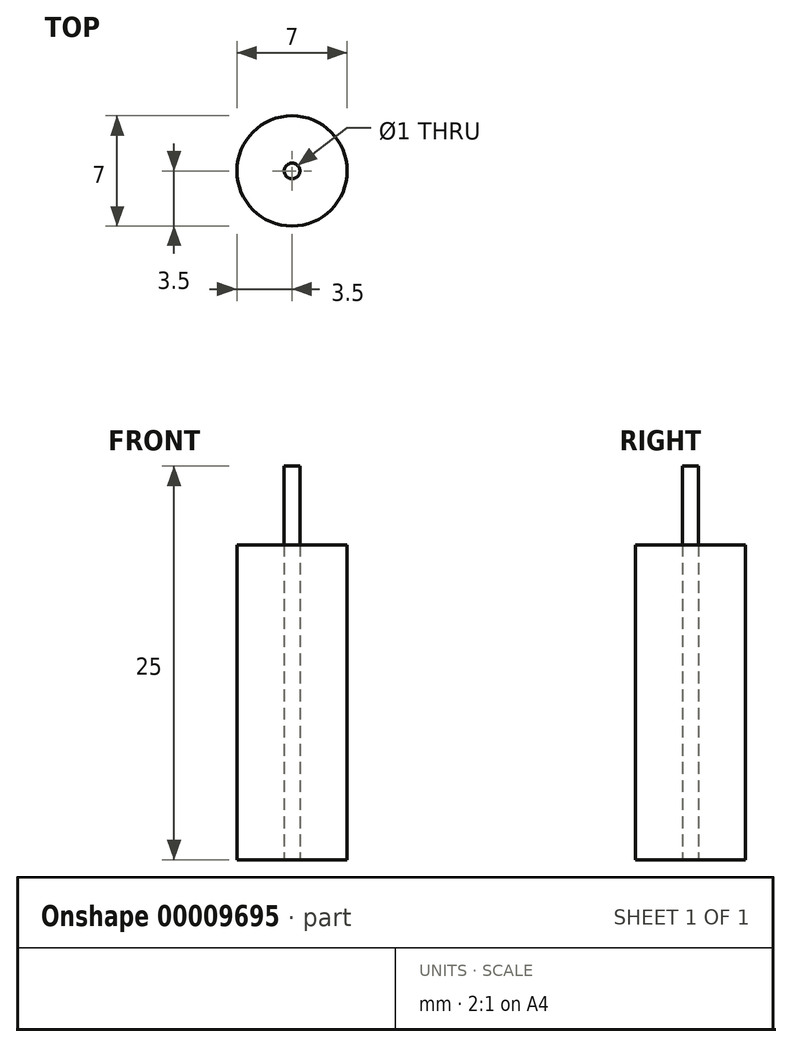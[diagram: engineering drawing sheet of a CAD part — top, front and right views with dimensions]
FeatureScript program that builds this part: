
annotation { "Feature Type Name" : "Feature", "Feature Type Description" : "" }
export const myFeature = defineFeature(function(context is Context, id is Id, definition is map)
    precondition{}
    {
        {
            var Q0;
            Q0=qCreatedBy(makeId("Top.planeOp"),FACE);
            var sketch = newSketch(context, id + "F0", { "sketchPlane" : qUnion([Q0])});
            skCircle(sketch, "E0", {"center": v(0, 0) * mm, "radius": 3.5 * mm});
            skCircle(sketch, "E1", {"center": v(0, 0) * mm, "radius": 0.5 * mm});
            skSolve(sketch);
        }
        {
            var Q0;
            Q0=qSketchRegion(id+"F0",true);
            extrude(context, id + "F1", {"entities" : qUnion([Q0]), "depth" : 20 * mm});
        }
        {
            var Q0;
            Q0=qCreatedBy(makeId("Top.planeOp"),FACE);
            var sketch = newSketch(context, id + "F2", { "sketchPlane" : qUnion([Q0])});
            skCircle(sketch, "E2", {"center": v(0, 0) * mm, "radius": 0.5 * mm});
            skSolve(sketch);
        }
        {
            var Q0;
            Q0=qSketchRegion(id+"F2",true);
            extrude(context, id + "F3", {"entities" : qUnion([Q0]), "depth" : 25 * mm});
        }
    });
